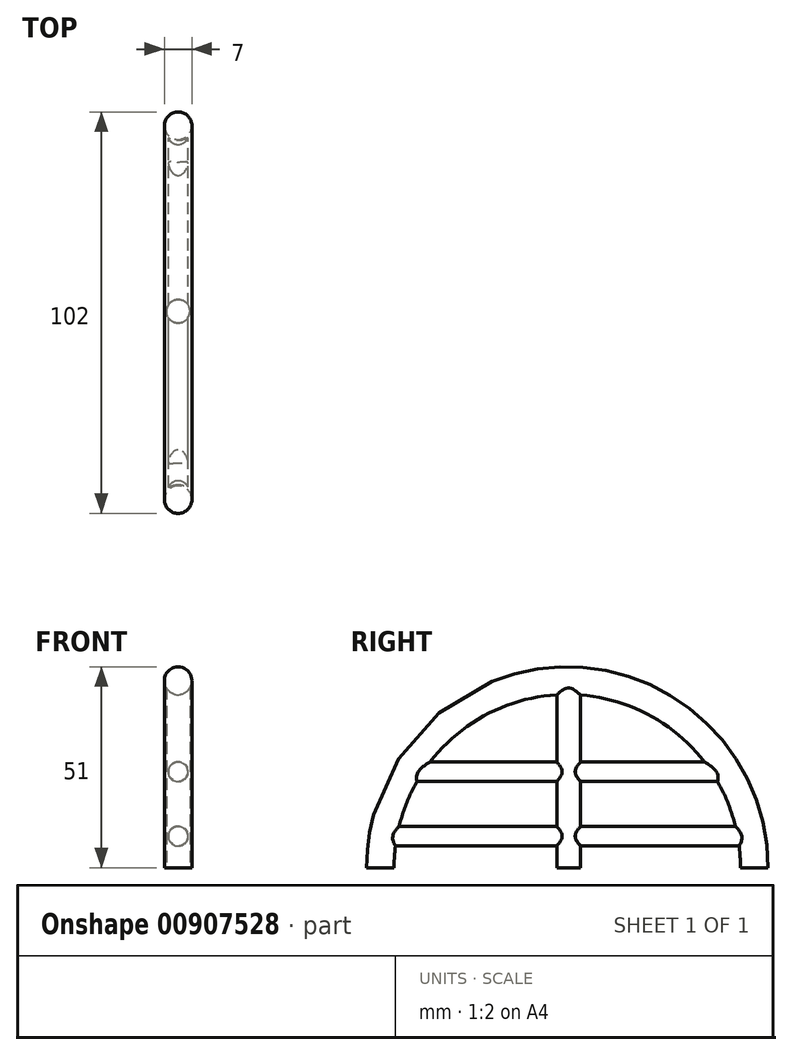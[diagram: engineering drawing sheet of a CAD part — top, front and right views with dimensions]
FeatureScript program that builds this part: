
annotation { "Feature Type Name" : "Feature", "Feature Type Description" : "" }
export const myFeature = defineFeature(function(context is Context, id is Id, definition is map)
    precondition{}
    {
        {
            var Q0;
            Q0=qCreatedBy(makeId("Right.planeOp"),FACE);
            var sketch = newSketch(context, id + "F0", { "sketchPlane" : qUnion([Q0])});
            skArc(sketch, "E0", {"start": v(49.65, 0) * mm, "mid": v(-0.35, 50.07) * mm, "end": v(-50.35, 0) * mm});
            skArc(sketch, "E1", {"start": v(44.65, 0) * mm, "mid": v(-0.35, 45) * mm, "end": v(-45.35, 0) * mm});
            skLineSegment(sketch, "E2", {"start": v(-45.35, 0) * mm, "end": v(-50.35, 0) * mm});
            skLineSegment(sketch, "E3", {"start": v(44.65, 0) * mm, "end": v(49.65, 0) * mm});
            skLineSegment(sketch, "E4", {"start": v(0, 0) * mm, "end": v(0, 63.24) * mm, "construction": true});
            skSolve(sketch);
        }
        {
            var Q0;
            Q0=qCreatedBy(makeId("Top.planeOp"),FACE);
            var sketch = newSketch(context, id + "F1", { "sketchPlane" : qUnion([Q0])});
            skCircle(sketch, "E5", {"center": v(0, -47.85) * mm, "radius": 3.5 * mm});
            skCircle(sketch, "E6.MirrorC", {"center": v(0, 47.15) * mm, "radius": 3.5 * mm});
            skSolve(sketch);
        }
        {
            var Q0;
            Q0=makeQuery(id+"F1.imprint","IMPRINT",FACE,{"disambiguationData":[TD([[makeQuery(id+"F1.imprint","IMPRINT",EDGE,{"derivedFrom":sQuery(id+"F1.wireOp",EDGE,"E5")}),1.0]])]});
            var Q1;
            Q1=sQuery(id+"F0.wireOp",EDGE,"E1");
            sweep(context, id + "F2", {"profiles" : qUnion([Q0]), "path" : qUnion([Q1])});
        }
        {
            var Q0;
            Q0=qCreatedBy(makeId("Top.planeOp"),FACE);
            var sketch = newSketch(context, id + "F3", { "sketchPlane" : qUnion([Q0])});
            skCircle(sketch, "E7", {"center": v(0, 0) * mm, "radius": 3 * mm});
            skSolve(sketch);
        }
        {
            var Q0;
            Q0=makeQuery(id+"F3.imprint","IMPRINT",FACE,{"disambiguationData":[TD([[makeQuery(id+"F3.imprint","IMPRINT",EDGE,{"derivedFrom":sQuery(id+"F3.wireOp",EDGE,"E7")}),1.0]])]});
            extrude(context, id + "F4", {"entities" : qUnion([Q0]), "operationType" : NewBodyOperationType.ADD, "depth" : 46 * mm, "offsetDistance" : 25 * mm});
        }
        {
            var Q0;
            Q0=qCreatedBy(makeId("Front.planeOp"),FACE);
            var sketch = newSketch(context, id + "F5", { "sketchPlane" : qUnion([Q0])});
            skCircle(sketch, "E8", {"center": v(0, 24.36) * mm, "radius": 2.5 * mm});
            skSolve(sketch);
        }
        {
            var Q0;
            Q0 = qSketchRegion(id + "F5", true);
            extrude(context, id + "F6", {"entities" : qUnion([Q0]), "operationType" : NewBodyOperationType.ADD, "endBound" : BoundingType.SYMMETRIC, "depth" : 81 * mm, "offsetDistance" : 25 * mm});
        }
        {
            var Q0;
            Q0=qCreatedBy(makeId("Front.planeOp"),FACE);
            var sketch = newSketch(context, id + "F7", { "sketchPlane" : qUnion([Q0])});
            skCircle(sketch, "E9", {"center": v(0, 8) * mm, "radius": 2.5 * mm});
            skSolve(sketch);
        }
        {
            var Q0;
            Q0=makeQuery(id+"F7.imprint","IMPRINT",FACE,{"disambiguationData":[TD([[makeQuery(id+"F7.imprint","IMPRINT",EDGE,{"derivedFrom":sQuery(id+"F7.wireOp",EDGE,"E9")}),1.0]])]});
            extrude(context, id + "F8", {"entities" : qUnion([Q0]), "operationType" : NewBodyOperationType.ADD, "endBound" : BoundingType.SYMMETRIC, "depth" : 90 * mm, "offsetDistance" : 25 * mm});
        }
    });
